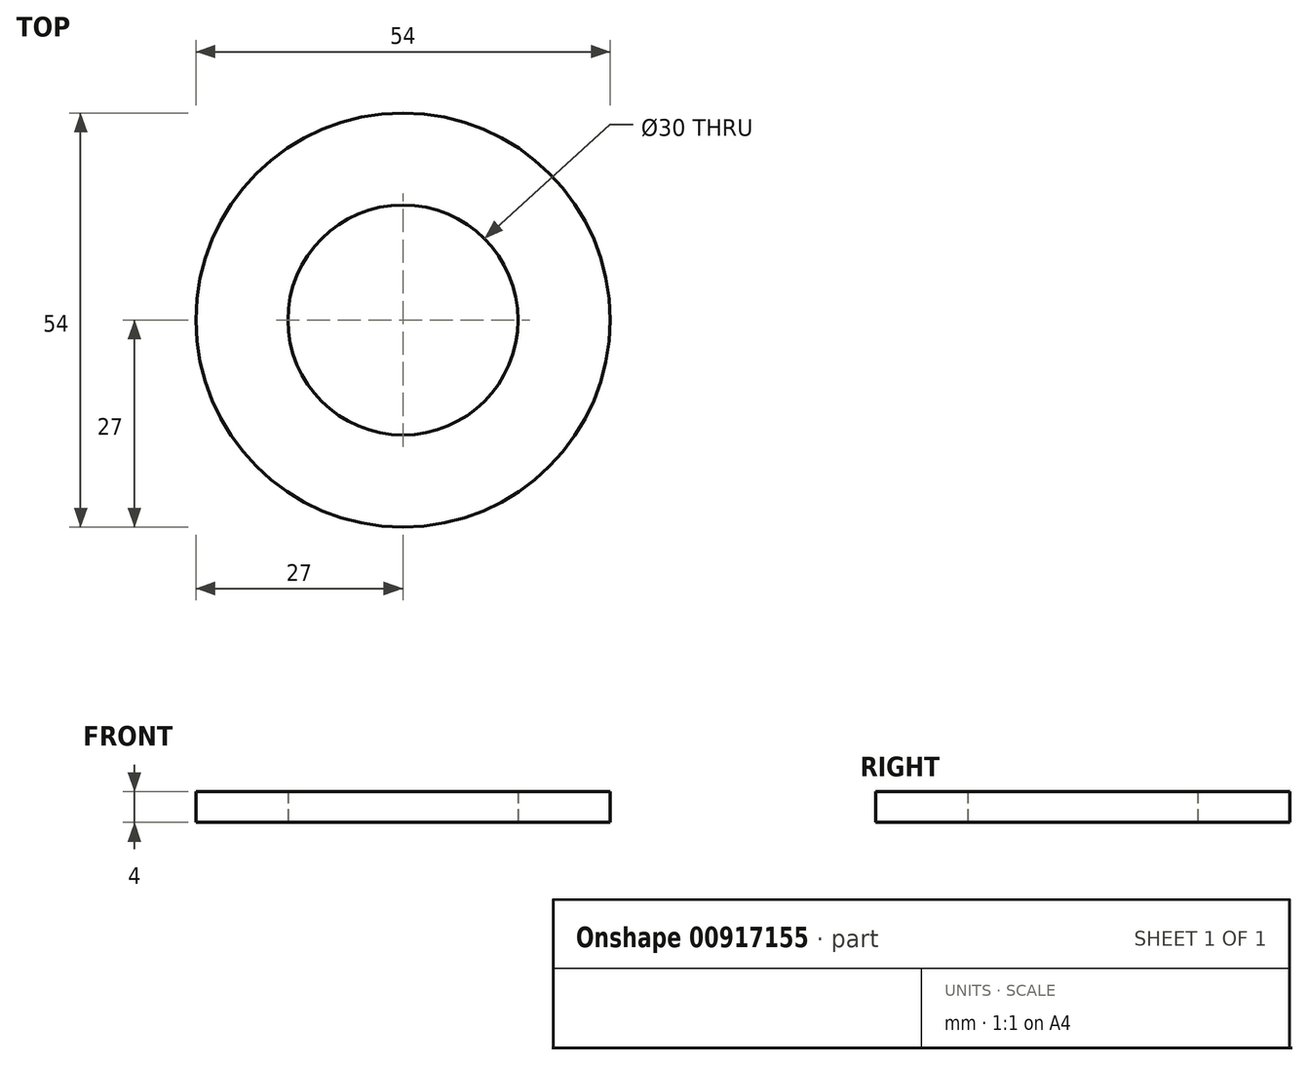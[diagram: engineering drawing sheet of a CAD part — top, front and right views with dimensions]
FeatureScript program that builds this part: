
annotation { "Feature Type Name" : "Feature", "Feature Type Description" : "" }
export const myFeature = defineFeature(function(context is Context, id is Id, definition is map)
    precondition{}
    {
        {
            var Q0;
            Q0=qCreatedBy(makeId("Top.planeOp"),FACE);
            var sketch = newSketch(context, id + "F0", { "sketchPlane" : qUnion([Q0])});
            skCircle(sketch, "E0", {"center": v(0, 0) * mm, "radius": 27 * mm});
            skCircle(sketch, "E1", {"center": v(0, 0) * mm, "radius": 15 * mm});
            skSolve(sketch);
        }
        {
            var Q0;
            Q0=makeQuery(id+"F0.imprint","IMPRINT",FACE,{"disambiguationData":[TD([[makeQuery(id+"F0.imprint","IMPRINT",EDGE,{"derivedFrom":sQuery(id+"F0.wireOp",EDGE,"E0")}),1.0]])]});
            extrude(context, id + "F1", {"entities" : qUnion([Q0]), "depth" : 4 * mm, "offsetDistance" : 25 * mm});
        }
    });
